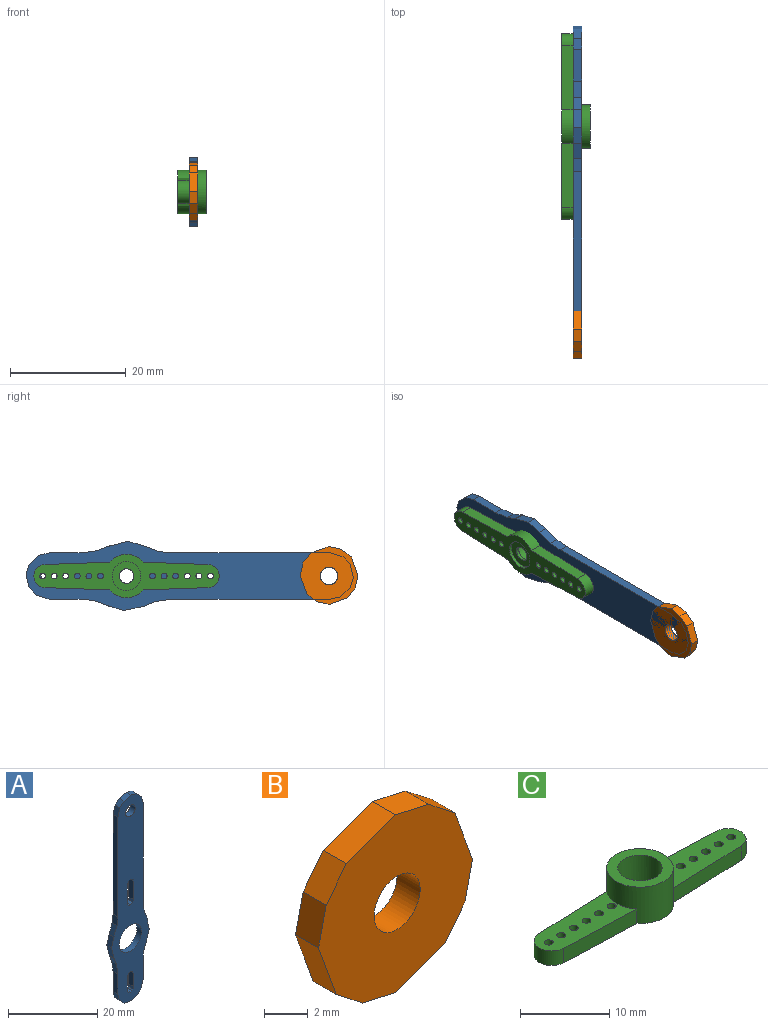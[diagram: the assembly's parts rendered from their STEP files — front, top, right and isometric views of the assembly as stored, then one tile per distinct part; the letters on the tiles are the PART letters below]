
ASSEMBLY  parts=3 mates=2
PART A: 58 faces, bbox 12x1.5x56.6 mm
  f0: plane 1.5x0.44mm, normal (0.29,0,0.96), area 0.7mm2, adj f1,f51,f55,f56
  f1: plane 1.5x0.42mm, normal (0.73,0,0.68), area 0.9mm2, adj f0,f2,f55,f56
  f2: plane 1.5x0.45mm, normal (0.97,0,0.23), area 0.7mm2, adj f1,f3,f55,f56
  f3: plane 3.7x1.5mm, normal (1,0,0), area 5.6mm2, adj f2,f4,f55,f56
  f4: plane 1.5x0.77mm, normal (0.91,0,-0.42), area 1.3mm2, adj f3,f5,f55,f56
  f5: plane 1.5x0.64mm, normal (0.34,0,-0.94), area 1mm2, adj f4,f6,f55,f56
  f6: plane 1.5x0.77mm, normal (-0.42,0,-0.91), area 1.3mm2, adj f5,f7,f55,f56
  f7: plane 1.5x0.64mm, normal (-0.94,0,-0.34), area 1mm2, adj f6,f8,f55,f56
  f8: plane 3.7x1.5mm, normal (-1,0,0), area 5.5mm2, adj f7,f9,f55,f56
  f9: plane 1.5x0.55mm, normal (-0.96,0,0.29), area 0.9mm2, adj f8,f10,f55,f56
  f10: plane 1.5x0.33mm, normal (-0.68,0,0.73), area 0.7mm2, adj f9,f51,f55,f56
  f11: plane 1.75x1.5mm, normal (-0.29,0,-0.96), area 2.7mm2, adj f12,f52,f55,f56
  f12: plane 2.25x1.5mm, normal (0.23,0,-0.97), area 3.5mm2, adj f11,f13,f55,f56
  f13: plane 1.5x1.33mm, normal (0.68,0,-0.73), area 2.7mm2, adj f12,f14,f55,f56
  f14: plane 2.21x1.5mm, normal (0.96,0,-0.29), area 3.5mm2, adj f13,f15,f55,f56
  f15: plane 5.53x1.5mm, normal (1,0,0), area 8.3mm2, adj f14,f16,f55,f56
  f16: plane 2.25x1.5mm, normal (0.99,0,-0.11), area 3.4mm2, adj f15,f17,f55,f56
  f17: plane 2.69x1.5mm, normal (0.94,0,-0.35), area 4.3mm2, adj f16,f18,f55,f56
  f18: plane 1.5x0.2mm, normal (-0.87,0,0.5), area 0.3mm2, adj f17,f19,f55,f56
  f19: plane 2.58x1.5mm, normal (0.95,0,-0.31), area 4.1mm2, adj f18,f20,f55,f56
  f20: plane 3.42x1.5mm, normal (0.98,0,0.21), area 5.2mm2, adj f19,f21,f55,f56
  f21: plane 2.09x1.5mm, normal (0.93,0,0.38), area 3.4mm2, adj f20,f22,f55,f56
  f22: plane 2.85x1.5mm, normal (0.99,0,0.14), area 4.3mm2, adj f21,f23,f55,f56
  f23: plane 27.35x1.5mm, normal (1,0,0), area 41mm2, adj f22,f24,f55,f56
  f24: plane 1.78x1.5mm, normal (0.97,0,0.23), area 2.7mm2, adj f23,f25,f55,f56
  f25: plane 1.68x1.58mm, normal (0.73,0,0.68), area 3.5mm2, adj f24,f26,f55,f56
  f26: plane 1.75x1.5mm, normal (0.29,0,0.96), area 2.7mm2, adj f25,f27,f55,f56
  f27: plane 2.25x1.5mm, normal (-0.23,0,0.97), area 3.5mm2, adj f26,f28,f55,f56
  f28: plane 1.5x1.33mm, normal (-0.68,0,0.73), area 2.7mm2, adj f27,f29,f55,f56
  f29: plane 2.21x1.5mm, normal (-0.96,0,0.29), area 3.5mm2, adj f28,f30,f55,f56
  f30: plane 27.35x1.5mm, normal (-1,0,0), area 41mm2, adj f29,f31,f55,f56
  f31: plane 2.25x1.5mm, normal (-0.99,0,0.11), area 3.4mm2, adj f30,f32,f55,f56
  f32: plane 2.69x1.5mm, normal (-0.94,0,0.35), area 4.3mm2, adj f31,f33,f55,f56
  f33: plane 2.69x1.5mm, normal (-0.96,0,0.27), area 4.2mm2, adj f32,f34,f55,f56
  f34: plane 3.34x1.5mm, normal (-0.97,0,-0.25), area 5.2mm2, adj f33,f35,f55,f56
  f35: plane 1.5x0.22mm, normal (0.87,0,0.5), area 0.4mm2, adj f34,f36,f55,f56
  f36: plane 2.09x1.5mm, normal (-0.93,0,-0.38), area 3.4mm2, adj f35,f37,f55,f56
  f37: plane 2.85x1.5mm, normal (-0.99,0,-0.14), area 4.3mm2, adj f36,f38,f55,f56
  f38: plane 5.53x1.5mm, normal (-1,0,0), area 8.3mm2, adj f37,f39,f55,f56
  f39: plane 1.78x1.5mm, normal (-0.97,0,-0.23), area 2.7mm2, adj f38,f52,f55,f56
  f40: plane 1.5x0.77mm, normal (-0.42,0,0.91), area 1.3mm2, adj f41,f53,f55,f56
  f41: plane 1.5x0.64mm, normal (0.34,0,0.94), area 1mm2, adj f40,f42,f55,f56
  f42: plane 1.5x0.77mm, normal (0.91,0,0.42), area 1.3mm2, adj f41,f43,f55,f56
  f43: plane 5x1.5mm, normal (1,0,0), area 7.5mm2, adj f42,f44,f55,f56
  f44: plane 1.5x0.45mm, normal (0.97,0,-0.23), area 0.7mm2, adj f43,f45,f55,f56
  f45: plane 1.5x0.42mm, normal (0.73,0,-0.68), area 0.9mm2, adj f44,f46,f55,f56
  f46: plane 1.5x0.44mm, normal (0.29,0,-0.96), area 0.7mm2, adj f45,f47,f55,f56
  f47: plane 1.5x0.56mm, normal (-0.23,0,-0.97), area 0.9mm2, adj f46,f48,f55,f56
  f48: plane 1.5x0.33mm, normal (-0.68,0,-0.73), area 0.7mm2, adj f47,f49,f55,f56
  f49: plane 1.5x0.55mm, normal (-0.96,0,-0.29), area 0.9mm2, adj f48,f50,f55,f56
  f50: plane 5x1.5mm, normal (-1,0,0), area 7.5mm2, adj f49,f53,f55,f56
  f51: plane 1.5x0.56mm, normal (-0.23,0,0.97), area 0.9mm2, adj f0,f10,f55,f56
  f52: plane 1.68x1.58mm, normal (-0.73,0,-0.68), area 3.5mm2, adj f11,f39,f55,f56
  f53: plane 1.5x0.64mm, normal (-0.94,0,0.34), area 1mm2, adj f40,f50,f55,f56
  f54: cylinder r=3.55mm len=7.1mm, axis (0,1,0), area 33.5mm2, adj f55,f56
  f55: plane 56.56x11.97mm, normal (0,-1,0), area 394.4mm2, adj f0,f1,f2,f3,f4,f5,f6,f7
  f56: plane 56.56x11.97mm, normal (0,1,0), area 394.4mm2, adj f0,f1,f2,f3,f4,f5,f6,f7
  f57: cylinder r=1.5mm len=3mm, axis (0,1,0), area 14.1mm2, adj f55,f56
PART B: 15 faces, bbox 10x1.5x10 mm
  f0: plane 3.2x1.5mm, normal (-0.94,0,-0.34), area 5.1mm2, adj f1,f11,f13,f14
  f1: plane 1.69x1.5mm, normal (-0.62,0,-0.79), area 3.2mm2, adj f0,f2,f13,f14
  f2: plane 2.16x1.5mm, normal (-0.22,0,-0.98), area 3.3mm2, adj f1,f3,f13,f14
  f3: plane 3.2x1.5mm, normal (0.34,0,-0.94), area 5.1mm2, adj f2,f4,f13,f14
  f4: plane 1.69x1.5mm, normal (0.79,0,-0.62), area 3.2mm2, adj f3,f5,f13,f14
  f5: plane 2.16x1.5mm, normal (0.98,0,-0.22), area 3.3mm2, adj f4,f6,f13,f14
  f6: plane 3.2x1.5mm, normal (0.94,0,0.34), area 5.1mm2, adj f5,f7,f13,f14
  f7: plane 1.69x1.5mm, normal (0.62,0,0.79), area 3.2mm2, adj f6,f8,f13,f14
  f8: plane 2.16x1.5mm, normal (0.22,0,0.98), area 3.3mm2, adj f7,f9,f13,f14
  f9: plane 3.2x1.5mm, normal (-0.34,0,0.94), area 5.1mm2, adj f8,f10,f13,f14
  f10: plane 1.69x1.5mm, normal (-0.79,0,0.62), area 3.2mm2, adj f9,f11,f13,f14
  f11: plane 2.16x1.5mm, normal (-0.98,0,0.22), area 3.3mm2, adj f0,f10,f13,f14
  f12: cylinder r=1.5mm len=3mm, axis (0,1,0), area 14.1mm2, adj f13,f14
  f13: plane 10x10mm, normal (0,-1,0), area 67.4mm2, adj f0,f1,f2,f3,f4,f5,f6,f7
  f14: plane 10x10mm, normal (0,1,0), area 67.4mm2, adj f0,f1,f2,f3,f4,f5,f6,f7
PART C: 28 faces, bbox 32x7.5x5 mm
  f0: cylinder r=2.5mm len=5mm, axis (0,0,1), area 62.8mm2, adj f11,f24
  f1: plane 13.11x4.79mm, normal (0,0,1), area 47.6mm2, adj f7,f8,f9,f10,f17,f18,f19,f20
  f2: plane 32x7.5mm, normal (0,0,-1), area 119.7mm2, adj f3,f4,f5,f7,f8,f9,f10,f12
  f3: plane 11.19x2mm, normal (0.04,-1,0), area 22.4mm2, adj f2,f4,f6,f7
  f4: cylinder r=2mm len=4mm, axis (0,0,-1), area 12.3mm2, adj f2,f3,f5,f6
  f5: plane 11.19x2mm, normal (0.04,1,0), area 22.4mm2, adj f2,f4,f6,f7
  f6: plane 13.11x4.79mm, normal (0,0,1), area 47.6mm2, adj f3,f4,f5,f7,f12,f13,f14,f15
  f7: cylinder r=3.75mm len=7.5mm, axis (0,0,1), area 97mm2, adj f1,f2,f3,f5,f6,f9,f10,f11
  f8: cylinder r=2mm len=4mm, axis (0,0,-1), area 12.3mm2, adj f1,f2,f9,f10
  f9: plane 11.19x2mm, normal (-0.04,-1,0), area 22.4mm2, adj f1,f2,f7,f8
  f10: plane 11.19x2mm, normal (-0.04,1,0), area 22.4mm2, adj f1,f2,f7,f8
  f11: plane 7.5x7.5mm, normal (0,0,1), area 24.5mm2, adj f0,f7
  f12: cylinder r=0.5mm len=2mm, axis (0,0,-1), area 6.3mm2, adj f2,f6
  f13: cylinder r=0.5mm len=2mm, axis (0,0,-1), area 6.3mm2, adj f2,f6
  f14: cylinder r=0.5mm len=2mm, axis (0,0,-1), area 6.3mm2, adj f2,f6
  f15: cylinder r=0.5mm len=2mm, axis (0,0,-1), area 6.3mm2, adj f2,f6
  f16: cylinder r=0.5mm len=2mm, axis (0,0,-1), area 6.3mm2, adj f2,f6
  f17: cylinder r=0.5mm len=2mm, axis (0,0,-1), area 6.3mm2, adj f1,f2
  f18: cylinder r=0.5mm len=2mm, axis (0,0,-1), area 6.3mm2, adj f1,f2
  f19: cylinder r=0.5mm len=2mm, axis (0,0,-1), area 6.3mm2, adj f1,f2
  f20: cylinder r=0.5mm len=2mm, axis (0,0,-1), area 6.3mm2, adj f1,f2
  f21: cylinder r=0.5mm len=2mm, axis (0,0,-1), area 6.3mm2, adj f1,f2
  f22: cylinder r=0.5mm len=2mm, axis (0,0,-1), area 6.3mm2, adj f1,f2
  f23: cylinder r=0.5mm len=2mm, axis (0,0,-1), area 6.3mm2, adj f2,f6
  f24: plane 5x5mm, normal (0,0,1), area 14.7mm2, adj f0,f27
  f25: cylinder r=2.5mm len=5mm, axis (0,0,-1), area 7.9mm2, adj f2,f26
  f26: plane 5x5mm, normal (0,0,-1), area 14.7mm2, adj f25,f27
  f27: cylinder r=1.25mm len=2.5mm, axis (0,0,-1), area 3.9mm2, adj f24,f26
PLACE A rot(axis=(0.58,0.58,-0.58),120deg) t=(0,-75.9,-133)mm
PLACE B rot(axis=(0.58,0.58,-0.58),120deg) t=(0,-68.33,-125.05)mm
PLACE C rot(axis=(-0.58,0.58,-0.58),120deg) t=(-3.5,0,0)mm
MATE fastened C.f0 <-> A.f54  axis (1,0,0) through (-1.5,0,0)mm
MATE fastened B.f12 <-> A.f57  axis (1,0,0) through (0,-35,0)mm
